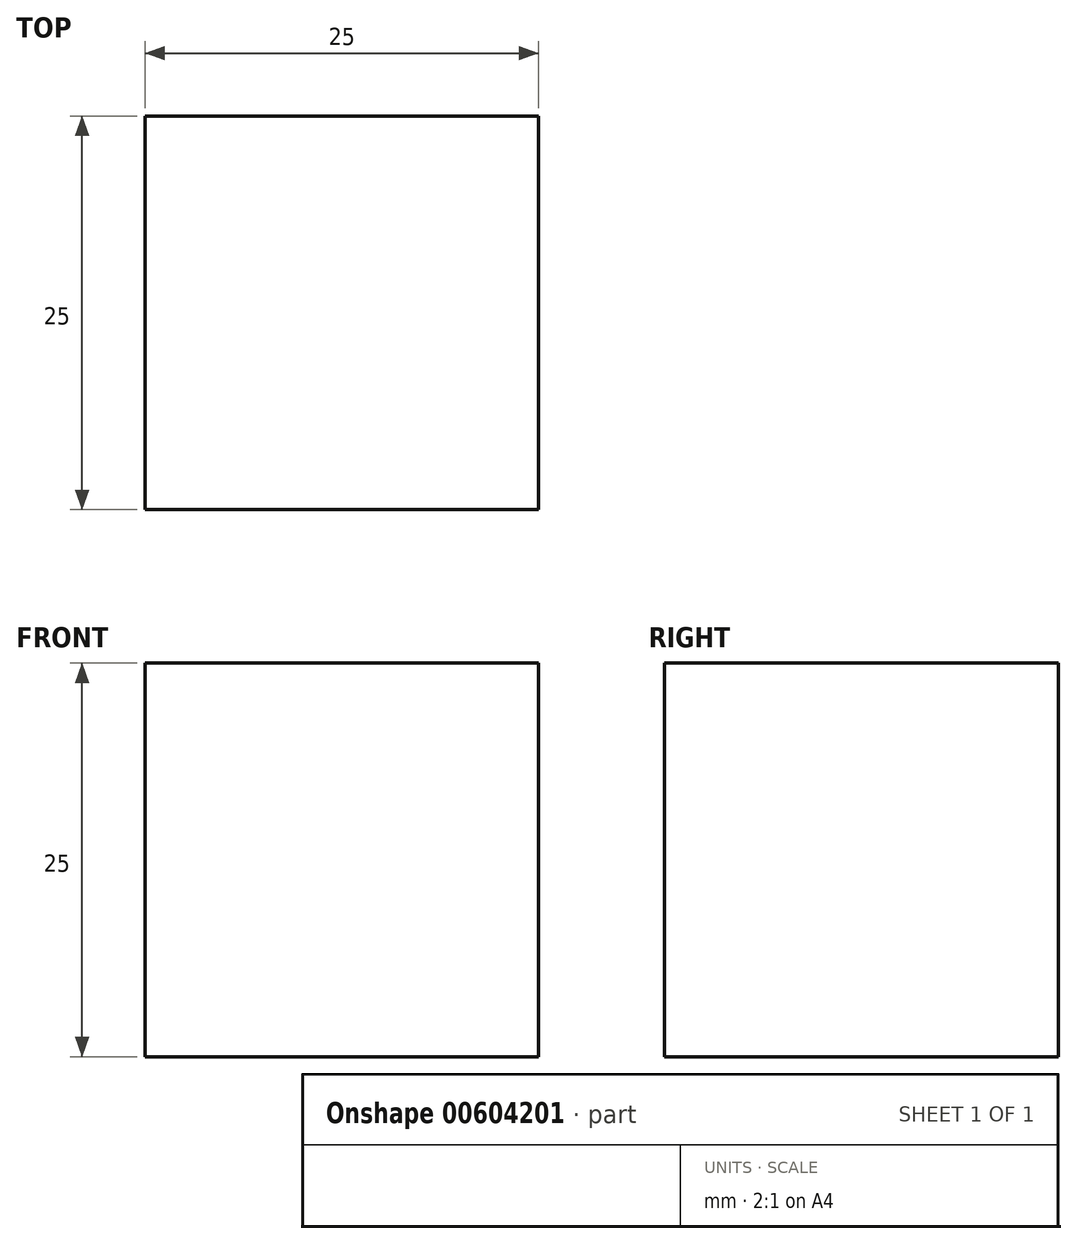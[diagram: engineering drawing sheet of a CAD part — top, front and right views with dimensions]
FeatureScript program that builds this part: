
annotation { "Feature Type Name" : "Feature", "Feature Type Description" : "" }
export const myFeature = defineFeature(function(context is Context, id is Id, definition is map)
    precondition{}
    {
        {
            var Q0;
            Q0=qCreatedBy(makeId("Top.planeOp"),FACE);
            var sketch = newSketch(context, id + "F0", { "sketchPlane" : qUnion([Q0])});
            skLineSegment(sketch, "E0.bottom", {"start": v(-12.5, 12.5) * mm, "end": v(12.5, 12.5) * mm});
            skLineSegment(sketch, "E0.top", {"start": v(-12.5, -12.5) * mm, "end": v(12.5, -12.5) * mm});
            skLineSegment(sketch, "E0.left", {"start": v(-12.5, 12.5) * mm, "end": v(-12.5, -12.5) * mm});
            skLineSegment(sketch, "E0.right", {"start": v(12.5, 12.5) * mm, "end": v(12.5, -12.5) * mm});
            skSolve(sketch);
        }
        {
            var Q0;
            Q0 = qSketchRegion(id + "F0", true);
            extrude(context, id + "F1", {"entities" : qUnion([Q0]), "depth" : 25 * mm, "offsetDistance" : 25 * mm});
        }
        {
            var Q0;
            Q0=makeQuery(id+"F1.opExtrude","SWEPT_BODY",BODY,{"disambiguationData":[OSD([sQuery(id+"F0.wireOp",EDGE,"E0.bottom"),sQuery(id+"F0.wireOp",EDGE,"E0.top"),sQuery(id+"F0.wireOp",EDGE,"E0.left"),sQuery(id+"F0.wireOp",EDGE,"E0.right")])]});
            transform(context, id + "F2", {"entities" : qUnion([Q0]), "transformType" : TransformType.TRANSLATION_3D, "dx" : 0 * mm, "dy" : 0 * mm, "dz" : 0 * mm, "makeCopy" : true});
        }
        {
            var Q0;
            Q0=makeQuery(id+"F2.opPattern","COPY",BODY,{"derivedFrom":makeQuery(id+"F1.opExtrude","SWEPT_BODY",BODY,{"disambiguationData":[OSD([sQuery(id+"F0.wireOp",EDGE,"E0.bottom"),sQuery(id+"F0.wireOp",EDGE,"E0.top"),sQuery(id+"F0.wireOp",EDGE,"E0.left"),sQuery(id+"F0.wireOp",EDGE,"E0.right")])]}),"instanceName":"1"});
            deleteBodies(context, id + "F3", {"entities" : qUnion([Q0])});
        }
    });
